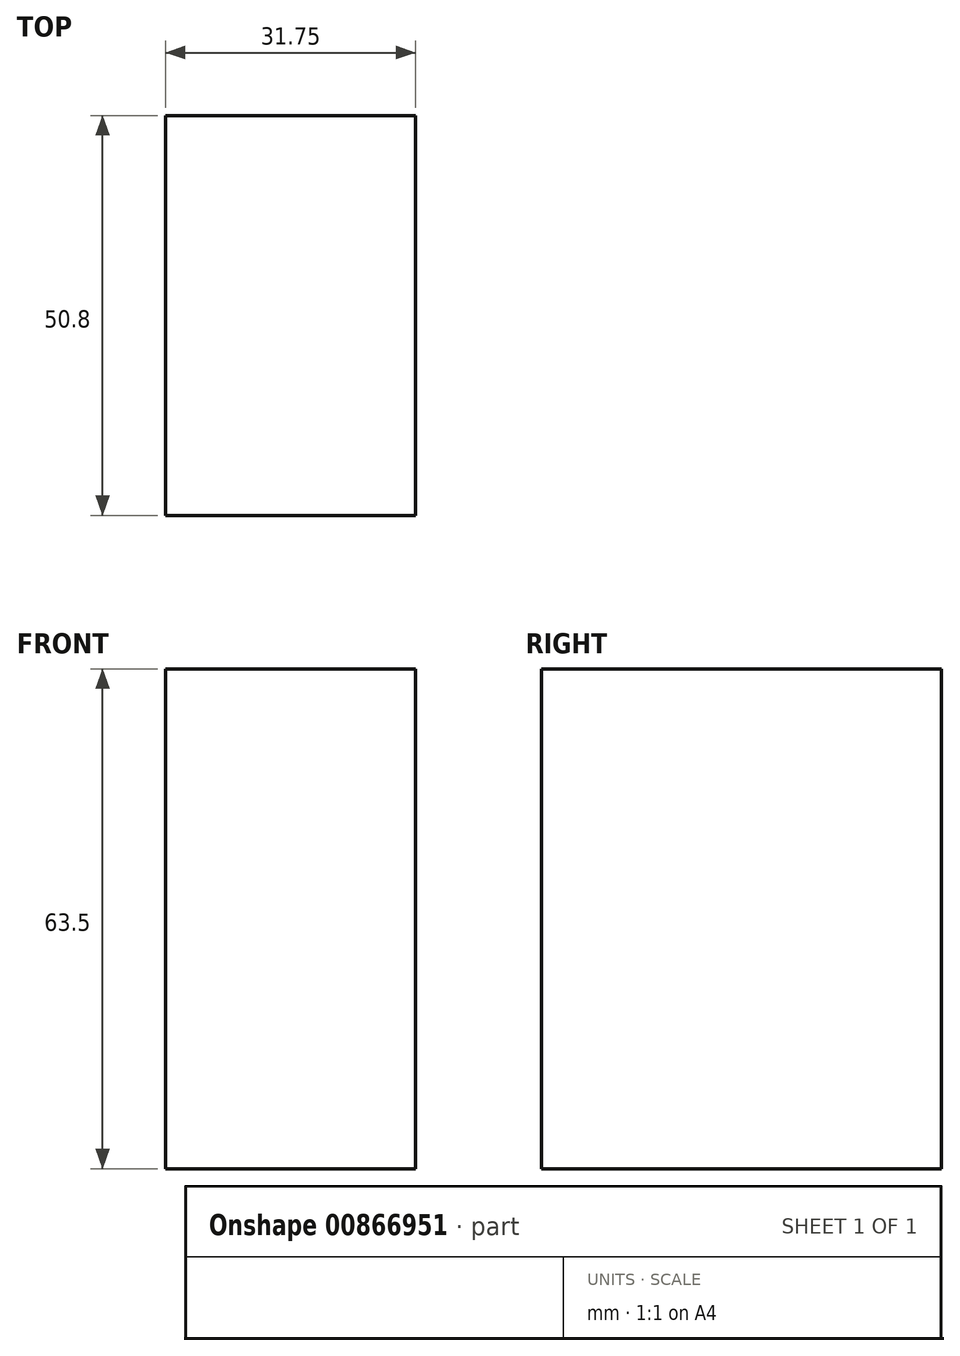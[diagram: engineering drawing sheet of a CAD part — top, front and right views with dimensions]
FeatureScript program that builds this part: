
annotation { "Feature Type Name" : "Feature", "Feature Type Description" : "" }
export const myFeature = defineFeature(function(context is Context, id is Id, definition is map)
    precondition{}
    {
        {
            var Q0;
            Q0=qCreatedBy(makeId("Top.planeOp"),FACE);
            var sketch = newSketch(context, id + "F0", { "sketchPlane" : qUnion([Q0])});
            skLineSegment(sketch, "E0.bottom", {"start": v(0, 0) * mm, "end": v(31.75, 0) * mm});
            skLineSegment(sketch, "E0.top", {"start": v(0, 50.8) * mm, "end": v(31.75, 50.8) * mm});
            skLineSegment(sketch, "E0.left", {"start": v(0, 0) * mm, "end": v(0, 50.8) * mm});
            skLineSegment(sketch, "E0.right", {"start": v(31.75, 0) * mm, "end": v(31.75, 50.8) * mm});
            skSolve(sketch);
        }
        {
            var Q0;
            Q0=makeQuery(id+"F0.imprint","IMPRINT",FACE,{"disambiguationData":[TD([[makeQuery(id+"F0.imprint","IMPRINT",EDGE,{"derivedFrom":sQuery(id+"F0.wireOp",EDGE,"E0.bottom")}),1.0]])]});
            extrude(context, id + "F1", {"entities" : qUnion([Q0]), "depth" : 63.5 * mm, "offsetDistance" : 25.4 * mm});
        }
    });
